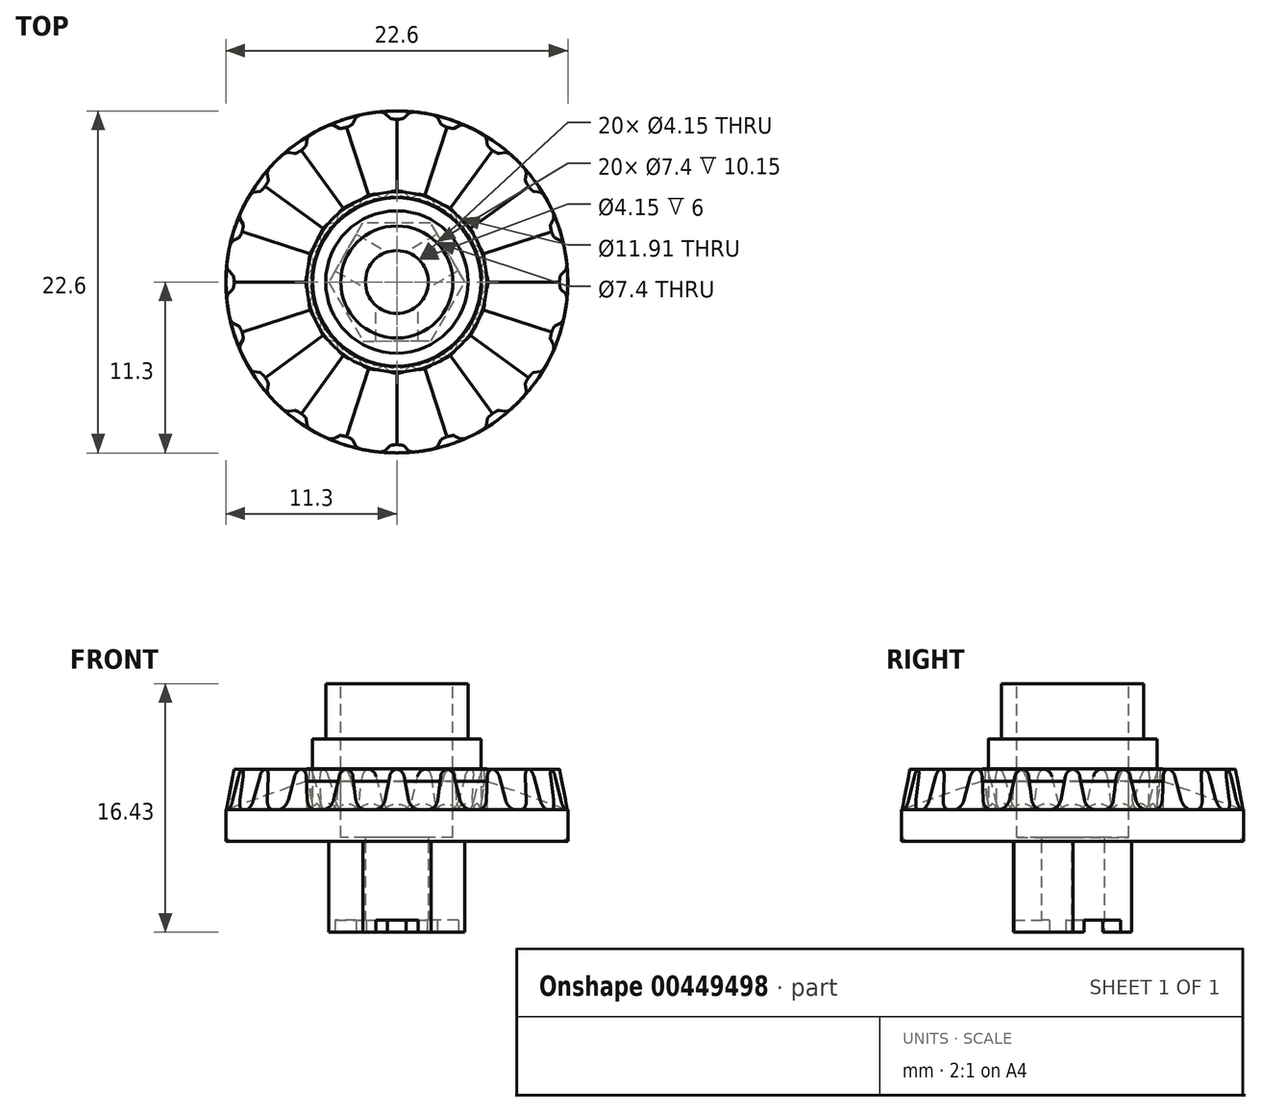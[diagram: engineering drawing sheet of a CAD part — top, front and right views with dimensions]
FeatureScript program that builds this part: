
annotation { "Feature Type Name" : "Feature", "Feature Type Description" : "" }
export const myFeature = defineFeature(function(context is Context, id is Id, definition is map)
    precondition{}
    {
        {
            var Q0;
            Q0=qCreatedBy(makeId("Top.planeOp"),FACE);
            var sketch = newSketch(context, id + "F0", { "sketchPlane" : qUnion([Q0])});
            skCircle(sketch, "E0", {"center": v(0, 0) * mm, "radius": 11.3 * mm});
            skSolve(sketch);
        }
        {
            var Q0;
            Q0 = qSketchRegion(id + "F0", true);
            extrude(context, id + "F1", {"entities" : qUnion([Q0]), "depth" : 2.1 * mm});
        }
        {
            var Q0;
            Q0=makeQuery(id+"F1.opExtrude","CAP_FACE",FACE,{"disambiguationData":[OSD([sQuery(id+"F0.wireOp",EDGE,"E0")])],"isStart":false});
            var sketch = newSketch(context, id + "F2", { "sketchPlane" : qUnion([Q0])});
            skCircle(sketch, "E1", {"center": v(0, 0) * mm, "radius": 5.58 * mm});
            skSolve(sketch);
        }
        {
            var Q0;
            Q0 = qSketchRegion(id + "F2", true);
            extrude(context, id + "F3", {"entities" : qUnion([Q0]), "operationType" : NewBodyOperationType.ADD, "depth" : 4.67 * mm});
        }
        {
            var Q0;
            Q0=makeQuery(id+"F3.opExtrude","CAP_FACE",FACE,{"disambiguationData":[OSD([sQuery(id+"F2.wireOp",EDGE,"E1")])],"isStart":false});
            var sketch = newSketch(context, id + "F4", { "sketchPlane" : qUnion([Q0])});
            skCircle(sketch, "E2", {"center": v(0, 0) * mm, "radius": 4.7 * mm});
            skSolve(sketch);
        }
        {
            var Q0;
            Q0 = qSketchRegion(id + "F4", true);
            extrude(context, id + "F5", {"entities" : qUnion([Q0]), "operationType" : NewBodyOperationType.ADD, "depth" : 3.66 * mm});
        }
        {
            var Q0;
            Q0=makeQuery(id+"F1.opExtrude","CAP_FACE",FACE,{"disambiguationData":[OSD([sQuery(id+"F0.wireOp",EDGE,"E0")])],"isStart":false});
            var sketch = newSketch(context, id + "F6", { "sketchPlane" : qUnion([Q0])});
            skLineSegment(sketch, "E3.bottom", {"start": v(-0.9, 5.5) * mm, "end": v(0.9, 5.5) * mm});
            skLineSegment(sketch, "E3.top", {"start": v(-0.9, 11.26) * mm, "end": v(0.9, 11.26) * mm});
            skLineSegment(sketch, "E3.left", {"start": v(-0.9, 5.5) * mm, "end": v(-0.9, 11.26) * mm});
            skLineSegment(sketch, "E3.right", {"start": v(0.9, 5.5) * mm, "end": v(0.9, 11.26) * mm});
            skSolve(sketch);
        }
        {
            var Q0;
            Q0 = qSketchRegion(id + "F6", true);
            extrude(context, id + "F7", {"entities" : qUnion([Q0]), "operationType" : NewBodyOperationType.ADD, "depth" : 2.7 * mm, "hasDraft" : true, "draftAngle" : 10.8 * degree, "draftPullDirection" : true});
        }
        {
            var Q0;
            Q0=makeQuery(id+"F1.opExtrude","SWEPT_BODY",BODY,{"disambiguationData":[OSD([sQuery(id+"F0.wireOp",EDGE,"E0")])]});
            var Q1;
            Q1=makeQuery(id+"F3.opExtrude","SWEPT_FACE",FACE,{"disambiguationData":[OSD([sQuery(id+"F2.wireOp",EDGE,"E1")])]});
            circularPattern(context, id + "F8", {"entities" : qUnion([Q0]), "axis" : qUnion([Q1]), "angle" : 360 * degree, "instanceCount" : 20, "equalSpace" : true});
        }
        {
            var Q0;
            {var subQ0=sQuery(id+"F0.wireOp",EDGE,"E0");var subQ1=makeQuery(id+"F1.opExtrude","CAP_FACE",FACE,{"disambiguationData":[OSD([subQ0])],"isStart":false});Q0=makeQuery(id+"F8.opPattern","COPY",FACE,{"derivedFrom":makeQuery(id+"F7.boolean.opBoolean","SPLIT",FACE,{"disambiguationData":[TD([makeQuery(id+"F1.opExtrude","SWEPT_FACE",FACE,{"disambiguationData":[OSD([subQ0])]}),subQ1,makeQuery(id+"F3.opExtrude","SWEPT_FACE",FACE,{"disambiguationData":[OSD([sQuery(id+"F2.wireOp",EDGE,"E1")])]}),makeQuery(id+"F7.opExtrude","SWEPT_FACE",FACE,{"disambiguationData":[OSD([sQuery(id+"F6.wireOp",EDGE,"E3.bottom")])]}),makeQuery(id+"F7.opExtrude","SWEPT_FACE",FACE,{"disambiguationData":[OSD([sQuery(id+"F6.wireOp",EDGE,"E3.top")])]}),makeQuery(id+"F7.opExtrude","SWEPT_FACE",FACE,{"disambiguationData":[OSD([sQuery(id+"F6.wireOp",EDGE,"E3.left")])]}),makeQuery(id+"F7.opExtrude","SWEPT_FACE",FACE,{"disambiguationData":[OSD([sQuery(id+"F6.wireOp",EDGE,"E3.right")])]})])],"derivedFrom":subQ1}),"instanceName":"11"});}
            var sketch = newSketch(context, id + "F9", { "sketchPlane" : qUnion([Q0])});
            skCircle(sketch, "E4", {"center": v(0, 0) * mm, "radius": 5.96 * mm});
            skSolve(sketch);
        }
        {
            var Q0;
            Q0 = qSketchRegion(id + "F9", true);
            extrude(context, id + "F10", {"entities" : qUnion([Q0]), "depth" : 2.7 * mm});
        }
        {
            var Q0;
            Q0=makeQuery(id+"F8.opPattern","COPY",EDGE,{"derivedFrom":makeQuery(id+"F7.opExtrude","CAP_EDGE",EDGE,{"disambiguationData":[OSD([sQuery(id+"F6.wireOp",EDGE,"E3.left")])],"isStart":false}),"instanceName":"1"});
            var Q1;
            Q1=makeQuery(id+"F8.opPattern","COPY",EDGE,{"derivedFrom":makeQuery(id+"F7.opExtrude","CAP_EDGE",EDGE,{"disambiguationData":[OSD([sQuery(id+"F6.wireOp",EDGE,"E3.right")])],"isStart":false}),"instanceName":"1"});
            var Q2;
            Q2=makeQuery(id+"F8.opPattern","COPY",EDGE,{"derivedFrom":makeQuery(id+"F7.opExtrude","CAP_EDGE",EDGE,{"disambiguationData":[OSD([sQuery(id+"F6.wireOp",EDGE,"E3.left")])],"isStart":false}),"instanceName":"2"});
            var Q3;
            Q3=makeQuery(id+"F8.opPattern","COPY",EDGE,{"derivedFrom":makeQuery(id+"F7.opExtrude","CAP_EDGE",EDGE,{"disambiguationData":[OSD([sQuery(id+"F6.wireOp",EDGE,"E3.right")])],"isStart":false}),"instanceName":"2"});
            var Q4;
            Q4=makeQuery(id+"F8.opPattern","COPY",EDGE,{"derivedFrom":makeQuery(id+"F7.opExtrude","CAP_EDGE",EDGE,{"disambiguationData":[OSD([sQuery(id+"F6.wireOp",EDGE,"E3.left")])],"isStart":false}),"instanceName":"3"});
            var Q5;
            Q5=makeQuery(id+"F8.opPattern","COPY",EDGE,{"derivedFrom":makeQuery(id+"F7.opExtrude","CAP_EDGE",EDGE,{"disambiguationData":[OSD([sQuery(id+"F6.wireOp",EDGE,"E3.right")])],"isStart":false}),"instanceName":"3"});
            var Q6;
            Q6=makeQuery(id+"F7.opExtrude","CAP_EDGE",EDGE,{"disambiguationData":[OSD([sQuery(id+"F6.wireOp",EDGE,"E3.right")])],"isStart":false});
            var Q7;
            Q7=makeQuery(id+"F7.opExtrude","CAP_EDGE",EDGE,{"disambiguationData":[OSD([sQuery(id+"F6.wireOp",EDGE,"E3.left")])],"isStart":false});
            var Q8;
            Q8=makeQuery(id+"F8.opPattern","COPY",EDGE,{"derivedFrom":makeQuery(id+"F7.opExtrude","CAP_EDGE",EDGE,{"disambiguationData":[OSD([sQuery(id+"F6.wireOp",EDGE,"E3.right")])],"isStart":false}),"instanceName":"19"});
            var Q9;
            Q9=makeQuery(id+"F8.opPattern","COPY",EDGE,{"derivedFrom":makeQuery(id+"F7.opExtrude","CAP_EDGE",EDGE,{"disambiguationData":[OSD([sQuery(id+"F6.wireOp",EDGE,"E3.left")])],"isStart":false}),"instanceName":"19"});
            var Q10;
            Q10=makeQuery(id+"F8.opPattern","COPY",EDGE,{"derivedFrom":makeQuery(id+"F7.opExtrude","CAP_EDGE",EDGE,{"disambiguationData":[OSD([sQuery(id+"F6.wireOp",EDGE,"E3.right")])],"isStart":false}),"instanceName":"4"});
            var Q11;
            Q11=makeQuery(id+"F8.opPattern","COPY",EDGE,{"derivedFrom":makeQuery(id+"F7.opExtrude","CAP_EDGE",EDGE,{"disambiguationData":[OSD([sQuery(id+"F6.wireOp",EDGE,"E3.left")])],"isStart":false}),"instanceName":"5"});
            var Q12;
            Q12=makeQuery(id+"F8.opPattern","COPY",EDGE,{"derivedFrom":makeQuery(id+"F7.opExtrude","CAP_EDGE",EDGE,{"disambiguationData":[OSD([sQuery(id+"F6.wireOp",EDGE,"E3.left")])],"isStart":false}),"instanceName":"6"});
            var Q13;
            Q13=makeQuery(id+"F8.opPattern","COPY",EDGE,{"derivedFrom":makeQuery(id+"F7.opExtrude","CAP_EDGE",EDGE,{"disambiguationData":[OSD([sQuery(id+"F6.wireOp",EDGE,"E3.right")])],"isStart":false}),"instanceName":"6"});
            var Q14;
            Q14=makeQuery(id+"F8.opPattern","COPY",EDGE,{"derivedFrom":makeQuery(id+"F7.opExtrude","CAP_EDGE",EDGE,{"disambiguationData":[OSD([sQuery(id+"F6.wireOp",EDGE,"E3.left")])],"isStart":false}),"instanceName":"7"});
            var Q15;
            Q15=makeQuery(id+"F8.opPattern","COPY",EDGE,{"derivedFrom":makeQuery(id+"F7.opExtrude","CAP_EDGE",EDGE,{"disambiguationData":[OSD([sQuery(id+"F6.wireOp",EDGE,"E3.right")])],"isStart":false}),"instanceName":"7"});
            var Q16;
            Q16=makeQuery(id+"F8.opPattern","COPY",EDGE,{"derivedFrom":makeQuery(id+"F7.opExtrude","CAP_EDGE",EDGE,{"disambiguationData":[OSD([sQuery(id+"F6.wireOp",EDGE,"E3.left")])],"isStart":false}),"instanceName":"8"});
            var Q17;
            Q17=makeQuery(id+"F8.opPattern","COPY",EDGE,{"derivedFrom":makeQuery(id+"F7.opExtrude","CAP_EDGE",EDGE,{"disambiguationData":[OSD([sQuery(id+"F6.wireOp",EDGE,"E3.right")])],"isStart":false}),"instanceName":"8"});
            var Q18;
            Q18=makeQuery(id+"F8.opPattern","COPY",EDGE,{"derivedFrom":makeQuery(id+"F7.opExtrude","CAP_EDGE",EDGE,{"disambiguationData":[OSD([sQuery(id+"F6.wireOp",EDGE,"E3.left")])],"isStart":false}),"instanceName":"9"});
            var Q19;
            Q19=makeQuery(id+"F8.opPattern","COPY",EDGE,{"derivedFrom":makeQuery(id+"F7.opExtrude","CAP_EDGE",EDGE,{"disambiguationData":[OSD([sQuery(id+"F6.wireOp",EDGE,"E3.right")])],"isStart":false}),"instanceName":"9"});
            var Q20;
            Q20=makeQuery(id+"F8.opPattern","COPY",EDGE,{"derivedFrom":makeQuery(id+"F7.opExtrude","CAP_EDGE",EDGE,{"disambiguationData":[OSD([sQuery(id+"F6.wireOp",EDGE,"E3.left")])],"isStart":false}),"instanceName":"10"});
            var Q21;
            Q21=makeQuery(id+"F8.opPattern","COPY",EDGE,{"derivedFrom":makeQuery(id+"F7.opExtrude","CAP_EDGE",EDGE,{"disambiguationData":[OSD([sQuery(id+"F6.wireOp",EDGE,"E3.right")])],"isStart":false}),"instanceName":"10"});
            var Q22;
            Q22=makeQuery(id+"F8.opPattern","COPY",EDGE,{"derivedFrom":makeQuery(id+"F7.opExtrude","CAP_EDGE",EDGE,{"disambiguationData":[OSD([sQuery(id+"F6.wireOp",EDGE,"E3.left")])],"isStart":false}),"instanceName":"11"});
            var Q23;
            Q23=makeQuery(id+"F8.opPattern","COPY",EDGE,{"derivedFrom":makeQuery(id+"F7.opExtrude","CAP_EDGE",EDGE,{"disambiguationData":[OSD([sQuery(id+"F6.wireOp",EDGE,"E3.right")])],"isStart":false}),"instanceName":"11"});
            var Q24;
            Q24=makeQuery(id+"F8.opPattern","COPY",EDGE,{"derivedFrom":makeQuery(id+"F7.opExtrude","CAP_EDGE",EDGE,{"disambiguationData":[OSD([sQuery(id+"F6.wireOp",EDGE,"E3.left")])],"isStart":false}),"instanceName":"12"});
            var Q25;
            Q25=makeQuery(id+"F8.opPattern","COPY",EDGE,{"derivedFrom":makeQuery(id+"F7.opExtrude","CAP_EDGE",EDGE,{"disambiguationData":[OSD([sQuery(id+"F6.wireOp",EDGE,"E3.right")])],"isStart":false}),"instanceName":"12"});
            var Q26;
            Q26=makeQuery(id+"F8.opPattern","COPY",EDGE,{"derivedFrom":makeQuery(id+"F7.opExtrude","CAP_EDGE",EDGE,{"disambiguationData":[OSD([sQuery(id+"F6.wireOp",EDGE,"E3.left")])],"isStart":false}),"instanceName":"13"});
            var Q27;
            Q27=makeQuery(id+"F8.opPattern","COPY",EDGE,{"derivedFrom":makeQuery(id+"F7.opExtrude","CAP_EDGE",EDGE,{"disambiguationData":[OSD([sQuery(id+"F6.wireOp",EDGE,"E3.right")])],"isStart":false}),"instanceName":"13"});
            var Q28;
            Q28=makeQuery(id+"F8.opPattern","COPY",EDGE,{"derivedFrom":makeQuery(id+"F7.opExtrude","CAP_EDGE",EDGE,{"disambiguationData":[OSD([sQuery(id+"F6.wireOp",EDGE,"E3.left")])],"isStart":false}),"instanceName":"14"});
            var Q29;
            Q29=makeQuery(id+"F8.opPattern","COPY",EDGE,{"derivedFrom":makeQuery(id+"F7.opExtrude","CAP_EDGE",EDGE,{"disambiguationData":[OSD([sQuery(id+"F6.wireOp",EDGE,"E3.right")])],"isStart":false}),"instanceName":"14"});
            var Q30;
            Q30=makeQuery(id+"F8.opPattern","COPY",EDGE,{"derivedFrom":makeQuery(id+"F7.opExtrude","CAP_EDGE",EDGE,{"disambiguationData":[OSD([sQuery(id+"F6.wireOp",EDGE,"E3.left")])],"isStart":false}),"instanceName":"15"});
            var Q31;
            Q31=makeQuery(id+"F8.opPattern","COPY",EDGE,{"derivedFrom":makeQuery(id+"F7.opExtrude","CAP_EDGE",EDGE,{"disambiguationData":[OSD([sQuery(id+"F6.wireOp",EDGE,"E3.right")])],"isStart":false}),"instanceName":"15"});
            var Q32;
            Q32=makeQuery(id+"F8.opPattern","COPY",EDGE,{"derivedFrom":makeQuery(id+"F7.opExtrude","CAP_EDGE",EDGE,{"disambiguationData":[OSD([sQuery(id+"F6.wireOp",EDGE,"E3.left")])],"isStart":false}),"instanceName":"16"});
            var Q33;
            Q33=makeQuery(id+"F8.opPattern","COPY",EDGE,{"derivedFrom":makeQuery(id+"F7.opExtrude","CAP_EDGE",EDGE,{"disambiguationData":[OSD([sQuery(id+"F6.wireOp",EDGE,"E3.right")])],"isStart":false}),"instanceName":"16"});
            var Q34;
            Q34=makeQuery(id+"F8.opPattern","COPY",EDGE,{"derivedFrom":makeQuery(id+"F7.opExtrude","CAP_EDGE",EDGE,{"disambiguationData":[OSD([sQuery(id+"F6.wireOp",EDGE,"E3.left")])],"isStart":false}),"instanceName":"17"});
            var Q35;
            Q35=makeQuery(id+"F8.opPattern","COPY",EDGE,{"derivedFrom":makeQuery(id+"F7.opExtrude","CAP_EDGE",EDGE,{"disambiguationData":[OSD([sQuery(id+"F6.wireOp",EDGE,"E3.right")])],"isStart":false}),"instanceName":"17"});
            var Q36;
            Q36=makeQuery(id+"F8.opPattern","COPY",EDGE,{"derivedFrom":makeQuery(id+"F7.opExtrude","CAP_EDGE",EDGE,{"disambiguationData":[OSD([sQuery(id+"F6.wireOp",EDGE,"E3.left")])],"isStart":false}),"instanceName":"18"});
            var Q37;
            Q37=makeQuery(id+"F8.opPattern","COPY",EDGE,{"derivedFrom":makeQuery(id+"F7.opExtrude","CAP_EDGE",EDGE,{"disambiguationData":[OSD([sQuery(id+"F6.wireOp",EDGE,"E3.right")])],"isStart":false}),"instanceName":"18"});
            var Q38;
            Q38=makeQuery(id+"F8.opPattern","COPY",EDGE,{"derivedFrom":makeQuery(id+"F7.opExtrude","CAP_EDGE",EDGE,{"disambiguationData":[OSD([sQuery(id+"F6.wireOp",EDGE,"E3.right")])],"isStart":false}),"instanceName":"5"});
            var Q39;
            Q39=makeQuery(id+"F8.opPattern","COPY",EDGE,{"derivedFrom":makeQuery(id+"F7.opExtrude","CAP_EDGE",EDGE,{"disambiguationData":[OSD([sQuery(id+"F6.wireOp",EDGE,"E3.left")])],"isStart":false}),"instanceName":"4"});
            fillet(context, id + "F11", {"entities" : qUnion([Q0, Q1, Q2, Q3, Q4, Q5, Q6, Q7, Q8, Q9, Q10, Q11, Q12, Q13, Q14, Q15, Q16, Q17, Q18, Q19, Q20, Q21, Q22, Q23, Q24, Q25, Q26, Q27, Q28, Q29, Q30, Q31, Q32, Q33, Q34, Q35, Q36, Q37, Q38, Q39]), "radius" : 0.6 * mm, "tangentPropagation" : true, "allowEdgeOverflow" : false});
        }
        {
            var Q0;
            Q0=makeQuery(id+"F8.opPattern","COPY",EDGE,{"derivedFrom":makeQuery(id+"F7.opExtrude","CAP_EDGE",EDGE,{"disambiguationData":[OSD([sQuery(id+"F6.wireOp",EDGE,"E3.right")])],"isStart":true}),"instanceName":"9"});
            var Q1;
            Q1=makeQuery(id+"F8.opPattern","COPY",EDGE,{"derivedFrom":makeQuery(id+"F7.opExtrude","CAP_EDGE",EDGE,{"disambiguationData":[OSD([sQuery(id+"F6.wireOp",EDGE,"E3.left")])],"isStart":true}),"instanceName":"10"});
            var Q2;
            Q2=makeQuery(id+"F8.opPattern","COPY",EDGE,{"derivedFrom":makeQuery(id+"F7.opExtrude","CAP_EDGE",EDGE,{"disambiguationData":[OSD([sQuery(id+"F6.wireOp",EDGE,"E3.right")])],"isStart":true}),"instanceName":"8"});
            var Q3;
            Q3=makeQuery(id+"F8.opPattern","COPY",EDGE,{"derivedFrom":makeQuery(id+"F7.opExtrude","CAP_EDGE",EDGE,{"disambiguationData":[OSD([sQuery(id+"F6.wireOp",EDGE,"E3.right")])],"isStart":true}),"instanceName":"7"});
            var Q4;
            Q4=makeQuery(id+"F8.opPattern","COPY",EDGE,{"derivedFrom":makeQuery(id+"F7.opExtrude","CAP_EDGE",EDGE,{"disambiguationData":[OSD([sQuery(id+"F6.wireOp",EDGE,"E3.right")])],"isStart":true}),"instanceName":"6"});
            var Q5;
            Q5=makeQuery(id+"F8.opPattern","COPY",EDGE,{"derivedFrom":makeQuery(id+"F7.opExtrude","CAP_EDGE",EDGE,{"disambiguationData":[OSD([sQuery(id+"F6.wireOp",EDGE,"E3.right")])],"isStart":true}),"instanceName":"5"});
            var Q6;
            Q6=makeQuery(id+"F8.opPattern","COPY",EDGE,{"derivedFrom":makeQuery(id+"F7.opExtrude","CAP_EDGE",EDGE,{"disambiguationData":[OSD([sQuery(id+"F6.wireOp",EDGE,"E3.left")])],"isStart":true}),"instanceName":"11"});
            var Q7;
            Q7=makeQuery(id+"F8.opPattern","COPY",EDGE,{"derivedFrom":makeQuery(id+"F7.opExtrude","CAP_EDGE",EDGE,{"disambiguationData":[OSD([sQuery(id+"F6.wireOp",EDGE,"E3.left")])],"isStart":true}),"instanceName":"12"});
            var Q8;
            Q8=makeQuery(id+"F8.opPattern","COPY",EDGE,{"derivedFrom":makeQuery(id+"F7.opExtrude","CAP_EDGE",EDGE,{"disambiguationData":[OSD([sQuery(id+"F6.wireOp",EDGE,"E3.left")])],"isStart":true}),"instanceName":"13"});
            var Q9;
            Q9=makeQuery(id+"F8.opPattern","COPY",EDGE,{"derivedFrom":makeQuery(id+"F7.opExtrude","CAP_EDGE",EDGE,{"disambiguationData":[OSD([sQuery(id+"F6.wireOp",EDGE,"E3.right")])],"isStart":true}),"instanceName":"11"});
            var Q10;
            Q10=makeQuery(id+"F8.opPattern","COPY",EDGE,{"derivedFrom":makeQuery(id+"F7.opExtrude","CAP_EDGE",EDGE,{"disambiguationData":[OSD([sQuery(id+"F6.wireOp",EDGE,"E3.right")])],"isStart":true}),"instanceName":"12"});
            var Q11;
            Q11=makeQuery(id+"F8.opPattern","COPY",EDGE,{"derivedFrom":makeQuery(id+"F7.opExtrude","CAP_EDGE",EDGE,{"disambiguationData":[OSD([sQuery(id+"F6.wireOp",EDGE,"E3.right")])],"isStart":true}),"instanceName":"10"});
            var Q12;
            Q12=makeQuery(id+"F8.opPattern","COPY",EDGE,{"derivedFrom":makeQuery(id+"F7.opExtrude","CAP_EDGE",EDGE,{"disambiguationData":[OSD([sQuery(id+"F6.wireOp",EDGE,"E3.left")])],"isStart":true}),"instanceName":"9"});
            var Q13;
            Q13=makeQuery(id+"F8.opPattern","COPY",EDGE,{"derivedFrom":makeQuery(id+"F7.opExtrude","CAP_EDGE",EDGE,{"disambiguationData":[OSD([sQuery(id+"F6.wireOp",EDGE,"E3.left")])],"isStart":true}),"instanceName":"8"});
            var Q14;
            Q14=makeQuery(id+"F8.opPattern","COPY",EDGE,{"derivedFrom":makeQuery(id+"F7.opExtrude","CAP_EDGE",EDGE,{"disambiguationData":[OSD([sQuery(id+"F6.wireOp",EDGE,"E3.left")])],"isStart":true}),"instanceName":"7"});
            var Q15;
            Q15=makeQuery(id+"F8.opPattern","COPY",EDGE,{"derivedFrom":makeQuery(id+"F7.opExtrude","CAP_EDGE",EDGE,{"disambiguationData":[OSD([sQuery(id+"F6.wireOp",EDGE,"E3.left")])],"isStart":true}),"instanceName":"6"});
            var Q16;
            Q16=makeQuery(id+"F8.opPattern","COPY",EDGE,{"derivedFrom":makeQuery(id+"F7.opExtrude","CAP_EDGE",EDGE,{"disambiguationData":[OSD([sQuery(id+"F6.wireOp",EDGE,"E3.left")])],"isStart":true}),"instanceName":"5"});
            var Q17;
            Q17=makeQuery(id+"F8.opPattern","COPY",EDGE,{"derivedFrom":makeQuery(id+"F7.opExtrude","CAP_EDGE",EDGE,{"disambiguationData":[OSD([sQuery(id+"F6.wireOp",EDGE,"E3.right")])],"isStart":true}),"instanceName":"4"});
            var Q18;
            Q18=makeQuery(id+"F8.opPattern","COPY",EDGE,{"derivedFrom":makeQuery(id+"F7.opExtrude","CAP_EDGE",EDGE,{"disambiguationData":[OSD([sQuery(id+"F6.wireOp",EDGE,"E3.left")])],"isStart":true}),"instanceName":"14"});
            var Q19;
            Q19=makeQuery(id+"F8.opPattern","COPY",EDGE,{"derivedFrom":makeQuery(id+"F7.opExtrude","CAP_EDGE",EDGE,{"disambiguationData":[OSD([sQuery(id+"F6.wireOp",EDGE,"E3.right")])],"isStart":true}),"instanceName":"13"});
            var Q20;
            Q20=makeQuery(id+"F8.opPattern","COPY",EDGE,{"derivedFrom":makeQuery(id+"F7.opExtrude","CAP_EDGE",EDGE,{"disambiguationData":[OSD([sQuery(id+"F6.wireOp",EDGE,"E3.left")])],"isStart":true}),"instanceName":"15"});
            var Q21;
            Q21=makeQuery(id+"F8.opPattern","COPY",EDGE,{"derivedFrom":makeQuery(id+"F7.opExtrude","CAP_EDGE",EDGE,{"disambiguationData":[OSD([sQuery(id+"F6.wireOp",EDGE,"E3.right")])],"isStart":true}),"instanceName":"14"});
            var Q22;
            Q22=makeQuery(id+"F8.opPattern","COPY",EDGE,{"derivedFrom":makeQuery(id+"F7.opExtrude","CAP_EDGE",EDGE,{"disambiguationData":[OSD([sQuery(id+"F6.wireOp",EDGE,"E3.right")])],"isStart":true}),"instanceName":"15"});
            var Q23;
            Q23=makeQuery(id+"F8.opPattern","COPY",EDGE,{"derivedFrom":makeQuery(id+"F7.opExtrude","CAP_EDGE",EDGE,{"disambiguationData":[OSD([sQuery(id+"F6.wireOp",EDGE,"E3.left")])],"isStart":true}),"instanceName":"16"});
            var Q24;
            Q24=makeQuery(id+"F8.opPattern","COPY",EDGE,{"derivedFrom":makeQuery(id+"F7.opExtrude","CAP_EDGE",EDGE,{"disambiguationData":[OSD([sQuery(id+"F6.wireOp",EDGE,"E3.right")])],"isStart":true}),"instanceName":"16"});
            var Q25;
            Q25=makeQuery(id+"F8.opPattern","COPY",EDGE,{"derivedFrom":makeQuery(id+"F7.opExtrude","CAP_EDGE",EDGE,{"disambiguationData":[OSD([sQuery(id+"F6.wireOp",EDGE,"E3.left")])],"isStart":true}),"instanceName":"17"});
            var Q26;
            Q26=makeQuery(id+"F8.opPattern","COPY",EDGE,{"derivedFrom":makeQuery(id+"F7.opExtrude","CAP_EDGE",EDGE,{"disambiguationData":[OSD([sQuery(id+"F6.wireOp",EDGE,"E3.left")])],"isStart":true}),"instanceName":"4"});
            var Q27;
            Q27=makeQuery(id+"F8.opPattern","COPY",EDGE,{"derivedFrom":makeQuery(id+"F7.opExtrude","CAP_EDGE",EDGE,{"disambiguationData":[OSD([sQuery(id+"F6.wireOp",EDGE,"E3.right")])],"isStart":true}),"instanceName":"3"});
            var Q28;
            Q28=makeQuery(id+"F8.opPattern","COPY",EDGE,{"derivedFrom":makeQuery(id+"F7.opExtrude","CAP_EDGE",EDGE,{"disambiguationData":[OSD([sQuery(id+"F6.wireOp",EDGE,"E3.right")])],"isStart":true}),"instanceName":"2"});
            var Q29;
            Q29=makeQuery(id+"F8.opPattern","COPY",EDGE,{"derivedFrom":makeQuery(id+"F7.opExtrude","CAP_EDGE",EDGE,{"disambiguationData":[OSD([sQuery(id+"F6.wireOp",EDGE,"E3.left")])],"isStart":true}),"instanceName":"3"});
            var Q30;
            Q30=makeQuery(id+"F8.opPattern","COPY",EDGE,{"derivedFrom":makeQuery(id+"F7.opExtrude","CAP_EDGE",EDGE,{"disambiguationData":[OSD([sQuery(id+"F6.wireOp",EDGE,"E3.right")])],"isStart":true}),"instanceName":"1"});
            var Q31;
            Q31=makeQuery(id+"F8.opPattern","COPY",EDGE,{"derivedFrom":makeQuery(id+"F7.opExtrude","CAP_EDGE",EDGE,{"disambiguationData":[OSD([sQuery(id+"F6.wireOp",EDGE,"E3.left")])],"isStart":true}),"instanceName":"2"});
            var Q32;
            Q32=makeQuery(id+"F8.opPattern","COPY",EDGE,{"derivedFrom":makeQuery(id+"F7.opExtrude","CAP_EDGE",EDGE,{"disambiguationData":[OSD([sQuery(id+"F6.wireOp",EDGE,"E3.left")])],"isStart":true}),"instanceName":"1"});
            var Q33;
            Q33=makeQuery(id+"F7.opExtrude","CAP_EDGE",EDGE,{"disambiguationData":[OSD([sQuery(id+"F6.wireOp",EDGE,"E3.right")])],"isStart":true});
            var Q34;
            Q34=makeQuery(id+"F7.opExtrude","CAP_EDGE",EDGE,{"disambiguationData":[OSD([sQuery(id+"F6.wireOp",EDGE,"E3.left")])],"isStart":true});
            var Q35;
            Q35=makeQuery(id+"F8.opPattern","COPY",EDGE,{"derivedFrom":makeQuery(id+"F7.opExtrude","CAP_EDGE",EDGE,{"disambiguationData":[OSD([sQuery(id+"F6.wireOp",EDGE,"E3.right")])],"isStart":true}),"instanceName":"19"});
            var Q36;
            Q36=makeQuery(id+"F8.opPattern","COPY",EDGE,{"derivedFrom":makeQuery(id+"F7.opExtrude","CAP_EDGE",EDGE,{"disambiguationData":[OSD([sQuery(id+"F6.wireOp",EDGE,"E3.left")])],"isStart":true}),"instanceName":"19"});
            var Q37;
            Q37=makeQuery(id+"F8.opPattern","COPY",EDGE,{"derivedFrom":makeQuery(id+"F7.opExtrude","CAP_EDGE",EDGE,{"disambiguationData":[OSD([sQuery(id+"F6.wireOp",EDGE,"E3.right")])],"isStart":true}),"instanceName":"18"});
            var Q38;
            Q38=makeQuery(id+"F8.opPattern","COPY",EDGE,{"derivedFrom":makeQuery(id+"F7.opExtrude","CAP_EDGE",EDGE,{"disambiguationData":[OSD([sQuery(id+"F6.wireOp",EDGE,"E3.left")])],"isStart":true}),"instanceName":"18"});
            var Q39;
            Q39=makeQuery(id+"F8.opPattern","COPY",EDGE,{"derivedFrom":makeQuery(id+"F7.opExtrude","CAP_EDGE",EDGE,{"disambiguationData":[OSD([sQuery(id+"F6.wireOp",EDGE,"E3.right")])],"isStart":true}),"instanceName":"17"});
            fillet(context, id + "F12", {"entities" : qUnion([Q0, Q1, Q2, Q3, Q4, Q5, Q6, Q7, Q8, Q9, Q10, Q11, Q12, Q13, Q14, Q15, Q16, Q17, Q18, Q19, Q20, Q21, Q22, Q23, Q24, Q25, Q26, Q27, Q28, Q29, Q30, Q31, Q32, Q33, Q34, Q35, Q36, Q37, Q38, Q39]), "radius" : 0.8 * mm, "tangentPropagation" : true, "allowEdgeOverflow" : false});
        }
        {
            var Q0;
            {var subQ0=sQuery(id+"F0.wireOp",EDGE,"E0");var subQ1=makeQuery(id+"F1.opExtrude","CAP_FACE",FACE,{"disambiguationData":[OSD([subQ0])],"isStart":false});Q0=makeQuery(id+"F8.opPattern","COPY",FACE,{"derivedFrom":makeQuery(id+"F7.boolean.opBoolean","SPLIT",FACE,{"disambiguationData":[TD([makeQuery(id+"F1.opExtrude","SWEPT_FACE",FACE,{"disambiguationData":[OSD([subQ0])]}),subQ1,makeQuery(id+"F3.opExtrude","SWEPT_FACE",FACE,{"disambiguationData":[OSD([sQuery(id+"F2.wireOp",EDGE,"E1")])]}),makeQuery(id+"F7.opExtrude","SWEPT_FACE",FACE,{"disambiguationData":[OSD([sQuery(id+"F6.wireOp",EDGE,"E3.bottom")])]}),makeQuery(id+"F7.opExtrude","SWEPT_FACE",FACE,{"disambiguationData":[OSD([sQuery(id+"F6.wireOp",EDGE,"E3.top")])]}),makeQuery(id+"F7.opExtrude","SWEPT_FACE",FACE,{"disambiguationData":[OSD([sQuery(id+"F6.wireOp",EDGE,"E3.left")])]}),makeQuery(id+"F7.opExtrude","SWEPT_FACE",FACE,{"disambiguationData":[OSD([sQuery(id+"F6.wireOp",EDGE,"E3.right")])]})])],"derivedFrom":subQ1}),"instanceName":"19"});}
            var sketch = newSketch(context, id + "F13", { "sketchPlane" : qUnion([Q0])});
            skCircle(sketch, "E5", {"center": v(0, 0) * mm, "radius": 5.96 * mm});
            skCircle(sketch, "E6", {"center": v(0, 0) * mm, "radius": 11.3 * mm});
            skSolve(sketch);
        }
        {
            var Q0;
            Q0 = qSketchRegion(id + "F13", true);
            extrude(context, id + "F14", {"entities" : qUnion([Q0]), "depth" : 2.03 * mm});
        }
        {
            var Q0;
            Q0=makeQuery(id+"F14.opExtrude","CAP_EDGE",EDGE,{"disambiguationData":[OSD([sQuery(id+"F13.wireOp",EDGE,"E6")])],"isStart":false});
            chamfer(context, id + "F15", {"entities" : qUnion([Q0]), "chamferType" : ChamferType.OFFSET_ANGLE, "width" : 5.72 * mm, "oppositeDirection" : false, "angle" : 19.52 * degree, "tangentPropagation" : true});
        }
        {
            var Q0;
            Q0=makeQuery(id+"F1.opExtrude","CAP_FACE",FACE,{"disambiguationData":[OSD([sQuery(id+"F0.wireOp",EDGE,"E0")])],"isStart":true});
            var sketch = newSketch(context, id + "F16", { "sketchPlane" : qUnion([Q0])});
            skCircle(sketch, "E7.cCircle", {"center": v(0, 0) * mm, "radius": 4.5 * mm, "construction": true});
            skLineSegment(sketch, "E7.0", {"start": v(2.23, -3.9) * mm, "end": v(-2.27, -3.89) * mm});
            skLineSegment(sketch, "E7.1", {"start": v(-2.27, -3.89) * mm, "end": v(-4.5, 0.02) * mm});
            skLineSegment(sketch, "E7.2", {"start": v(-4.5, 0.02) * mm, "end": v(-2.23, 3.9) * mm});
            skLineSegment(sketch, "E7.3", {"start": v(-2.23, 3.9) * mm, "end": v(2.27, 3.89) * mm});
            skLineSegment(sketch, "E7.4", {"start": v(2.27, 3.89) * mm, "end": v(4.5, -0.02) * mm});
            skLineSegment(sketch, "E7.5", {"start": v(4.5, -0.02) * mm, "end": v(2.23, -3.9) * mm});
            skSolve(sketch);
        }
        {
            var Q0;
            Q0 = qSketchRegion(id + "F16", true);
            extrude(context, id + "F17", {"entities" : qUnion([Q0]), "depth" : 6 * mm});
        }
        {
            var Q0;
            Q0=makeQuery(id+"F17.opExtrude","CAP_FACE",FACE,{"disambiguationData":[OSD([sQuery(id+"F16.wireOp",EDGE,"E7.0"),sQuery(id+"F16.wireOp",EDGE,"E7.1"),sQuery(id+"F16.wireOp",EDGE,"E7.2"),sQuery(id+"F16.wireOp",EDGE,"E7.3"),sQuery(id+"F16.wireOp",EDGE,"E7.4"),sQuery(id+"F16.wireOp",EDGE,"E7.5")])],"isStart":false});
            var sketch = newSketch(context, id + "F18", { "sketchPlane" : qUnion([Q0])});
            skCircle(sketch, "E8", {"center": v(0, 0) * mm, "radius": 2.08 * mm});
            skSolve(sketch);
        }
        {
            var Q0;
            Q0 = qSketchRegion(id + "F18", true);
            extrude(context, id + "F19", {"entities" : qUnion([Q0]), "operationType" : NewBodyOperationType.REMOVE, "oppositeDirection" : true, "depth" : 25 * mm});
        }
        {
            var Q0;
            Q0=makeQuery(id+"F8.opPattern","COPY",FACE,{"derivedFrom":makeQuery(id+"F5.opExtrude","CAP_FACE",FACE,{"disambiguationData":[OSD([sQuery(id+"F4.wireOp",EDGE,"E2")])],"isStart":false}),"instanceName":"16"});
            var sketch = newSketch(context, id + "F20", { "sketchPlane" : qUnion([Q0])});
            skCircle(sketch, "E9", {"center": v(0, 0) * mm, "radius": 3.7 * mm});
            skSolve(sketch);
        }
        {
            var Q0;
            Q0 = qSketchRegion(id + "F20", true);
            extrude(context, id + "F21", {"entities" : qUnion([Q0]), "operationType" : NewBodyOperationType.REMOVE, "oppositeDirection" : true, "depth" : 10.15 * mm});
        }
        {
            var Q0;
            Q0=makeQuery(id+"F1.opExtrude","CAP_EDGE",EDGE,{"disambiguationData":[OSD([sQuery(id+"F0.wireOp",EDGE,"E0")])],"isStart":true});
            var Q1;
            Q1=makeQuery(id+"F8.opPattern","COPY",EDGE,{"derivedFrom":makeQuery(id+"F1.opExtrude","CAP_EDGE",EDGE,{"disambiguationData":[OSD([sQuery(id+"F0.wireOp",EDGE,"E0")])],"isStart":true}),"instanceName":"19"});
            var Q2;
            Q2=makeQuery(id+"F8.opPattern","COPY",EDGE,{"derivedFrom":makeQuery(id+"F1.opExtrude","CAP_EDGE",EDGE,{"disambiguationData":[OSD([sQuery(id+"F0.wireOp",EDGE,"E0")])],"isStart":true}),"instanceName":"1"});
            var Q3;
            Q3=makeQuery(id+"F8.opPattern","COPY",EDGE,{"derivedFrom":makeQuery(id+"F1.opExtrude","CAP_EDGE",EDGE,{"disambiguationData":[OSD([sQuery(id+"F0.wireOp",EDGE,"E0")])],"isStart":true}),"instanceName":"3"});
            var Q4;
            Q4=makeQuery(id+"F8.opPattern","COPY",EDGE,{"derivedFrom":makeQuery(id+"F1.opExtrude","CAP_EDGE",EDGE,{"disambiguationData":[OSD([sQuery(id+"F0.wireOp",EDGE,"E0")])],"isStart":true}),"instanceName":"4"});
            var Q5;
            Q5=makeQuery(id+"F8.opPattern","COPY",EDGE,{"derivedFrom":makeQuery(id+"F1.opExtrude","CAP_EDGE",EDGE,{"disambiguationData":[OSD([sQuery(id+"F0.wireOp",EDGE,"E0")])],"isStart":true}),"instanceName":"5"});
            var Q6;
            Q6=makeQuery(id+"F8.opPattern","COPY",EDGE,{"derivedFrom":makeQuery(id+"F1.opExtrude","CAP_EDGE",EDGE,{"disambiguationData":[OSD([sQuery(id+"F0.wireOp",EDGE,"E0")])],"isStart":true}),"instanceName":"6"});
            var Q7;
            Q7=makeQuery(id+"F8.opPattern","COPY",EDGE,{"derivedFrom":makeQuery(id+"F1.opExtrude","CAP_EDGE",EDGE,{"disambiguationData":[OSD([sQuery(id+"F0.wireOp",EDGE,"E0")])],"isStart":true}),"instanceName":"7"});
            var Q8;
            Q8=makeQuery(id+"F8.opPattern","COPY",EDGE,{"derivedFrom":makeQuery(id+"F1.opExtrude","CAP_EDGE",EDGE,{"disambiguationData":[OSD([sQuery(id+"F0.wireOp",EDGE,"E0")])],"isStart":true}),"instanceName":"8"});
            var Q9;
            Q9=makeQuery(id+"F8.opPattern","COPY",EDGE,{"derivedFrom":makeQuery(id+"F1.opExtrude","CAP_EDGE",EDGE,{"disambiguationData":[OSD([sQuery(id+"F0.wireOp",EDGE,"E0")])],"isStart":true}),"instanceName":"9"});
            var Q10;
            Q10=makeQuery(id+"F8.opPattern","COPY",EDGE,{"derivedFrom":makeQuery(id+"F1.opExtrude","CAP_EDGE",EDGE,{"disambiguationData":[OSD([sQuery(id+"F0.wireOp",EDGE,"E0")])],"isStart":true}),"instanceName":"10"});
            var Q11;
            Q11=makeQuery(id+"F8.opPattern","COPY",EDGE,{"derivedFrom":makeQuery(id+"F1.opExtrude","CAP_EDGE",EDGE,{"disambiguationData":[OSD([sQuery(id+"F0.wireOp",EDGE,"E0")])],"isStart":true}),"instanceName":"11"});
            var Q12;
            Q12=makeQuery(id+"F8.opPattern","COPY",EDGE,{"derivedFrom":makeQuery(id+"F1.opExtrude","CAP_EDGE",EDGE,{"disambiguationData":[OSD([sQuery(id+"F0.wireOp",EDGE,"E0")])],"isStart":true}),"instanceName":"12"});
            var Q13;
            Q13=makeQuery(id+"F8.opPattern","COPY",EDGE,{"derivedFrom":makeQuery(id+"F1.opExtrude","CAP_EDGE",EDGE,{"disambiguationData":[OSD([sQuery(id+"F0.wireOp",EDGE,"E0")])],"isStart":true}),"instanceName":"13"});
            var Q14;
            Q14=makeQuery(id+"F8.opPattern","COPY",EDGE,{"derivedFrom":makeQuery(id+"F1.opExtrude","CAP_EDGE",EDGE,{"disambiguationData":[OSD([sQuery(id+"F0.wireOp",EDGE,"E0")])],"isStart":true}),"instanceName":"14"});
            var Q15;
            Q15=makeQuery(id+"F8.opPattern","COPY",EDGE,{"derivedFrom":makeQuery(id+"F1.opExtrude","CAP_EDGE",EDGE,{"disambiguationData":[OSD([sQuery(id+"F0.wireOp",EDGE,"E0")])],"isStart":true}),"instanceName":"15"});
            var Q16;
            Q16=makeQuery(id+"F8.opPattern","COPY",EDGE,{"derivedFrom":makeQuery(id+"F1.opExtrude","CAP_EDGE",EDGE,{"disambiguationData":[OSD([sQuery(id+"F0.wireOp",EDGE,"E0")])],"isStart":true}),"instanceName":"16"});
            var Q17;
            Q17=makeQuery(id+"F8.opPattern","COPY",EDGE,{"derivedFrom":makeQuery(id+"F1.opExtrude","CAP_EDGE",EDGE,{"disambiguationData":[OSD([sQuery(id+"F0.wireOp",EDGE,"E0")])],"isStart":true}),"instanceName":"17"});
            var Q18;
            Q18=makeQuery(id+"F8.opPattern","COPY",EDGE,{"derivedFrom":makeQuery(id+"F1.opExtrude","CAP_EDGE",EDGE,{"disambiguationData":[OSD([sQuery(id+"F0.wireOp",EDGE,"E0")])],"isStart":true}),"instanceName":"18"});
            fillet(context, id + "F22", {"entities" : qUnion([Q0, Q1, Q2, Q3, Q4, Q5, Q6, Q7, Q8, Q9, Q10, Q11, Q12, Q13, Q14, Q15, Q16, Q17, Q18]), "radius" : 0.5 * mm, "tangentPropagation" : true, "allowEdgeOverflow" : false});
        }
        {
            var Q0;
            Q0=makeQuery(id+"F17.opExtrude","CAP_FACE",FACE,{"disambiguationData":[OSD([sQuery(id+"F16.wireOp",EDGE,"E7.0"),sQuery(id+"F16.wireOp",EDGE,"E7.1"),sQuery(id+"F16.wireOp",EDGE,"E7.2"),sQuery(id+"F16.wireOp",EDGE,"E7.3"),sQuery(id+"F16.wireOp",EDGE,"E7.4"),sQuery(id+"F16.wireOp",EDGE,"E7.5")])],"isStart":false});
            var sketch = newSketch(context, id + "F23", { "sketchPlane" : qUnion([Q0])});
            skLineSegment(sketch, "E10.bottom", {"start": v(-1.4, 3.9) * mm, "end": v(1.4, 3.9) * mm});
            skLineSegment(sketch, "E10.top", {"start": v(-1.4, 0) * mm, "end": v(1.4, 0) * mm});
            skLineSegment(sketch, "E10.left", {"start": v(-1.4, 3.9) * mm, "end": v(-1.4, 0) * mm});
            skLineSegment(sketch, "E10.right", {"start": v(1.4, 3.9) * mm, "end": v(1.4, 0) * mm});
            skLineSegment(sketch, "E11.1.0", {"start": v(-4.08, -0.74) * mm, "end": v(-0.7, 1.21) * mm});
            skLineSegment(sketch, "E11.1.1", {"start": v(-2.68, -3.16) * mm, "end": v(-4.08, -0.74) * mm});
            skLineSegment(sketch, "E11.1.2", {"start": v(-2.68, -3.16) * mm, "end": v(0.7, -1.21) * mm});
            skLineSegment(sketch, "E11.1.3", {"start": v(0.7, -1.21) * mm, "end": v(-0.7, 1.21) * mm});
            skLineSegment(sketch, "E11.2.0", {"start": v(2.68, -3.16) * mm, "end": v(-0.7, -1.21) * mm});
            skLineSegment(sketch, "E11.2.1", {"start": v(4.08, -0.74) * mm, "end": v(2.68, -3.16) * mm});
            skLineSegment(sketch, "E11.2.2", {"start": v(4.08, -0.74) * mm, "end": v(0.7, 1.21) * mm});
            skLineSegment(sketch, "E11.2.3", {"start": v(0.7, 1.21) * mm, "end": v(-0.7, -1.21) * mm});
            skPoint(sketch, "E11.center", {"position": v(0, 0) * mm});
            skSolve(sketch);
        }
        {
            var Q0;
            Q0 = qSketchRegion(id + "F23", true);
            extrude(context, id + "F24", {"entities" : qUnion([Q0]), "operationType" : NewBodyOperationType.REMOVE, "oppositeDirection" : true, "depth" : 0.8 * mm});
        }
    });
